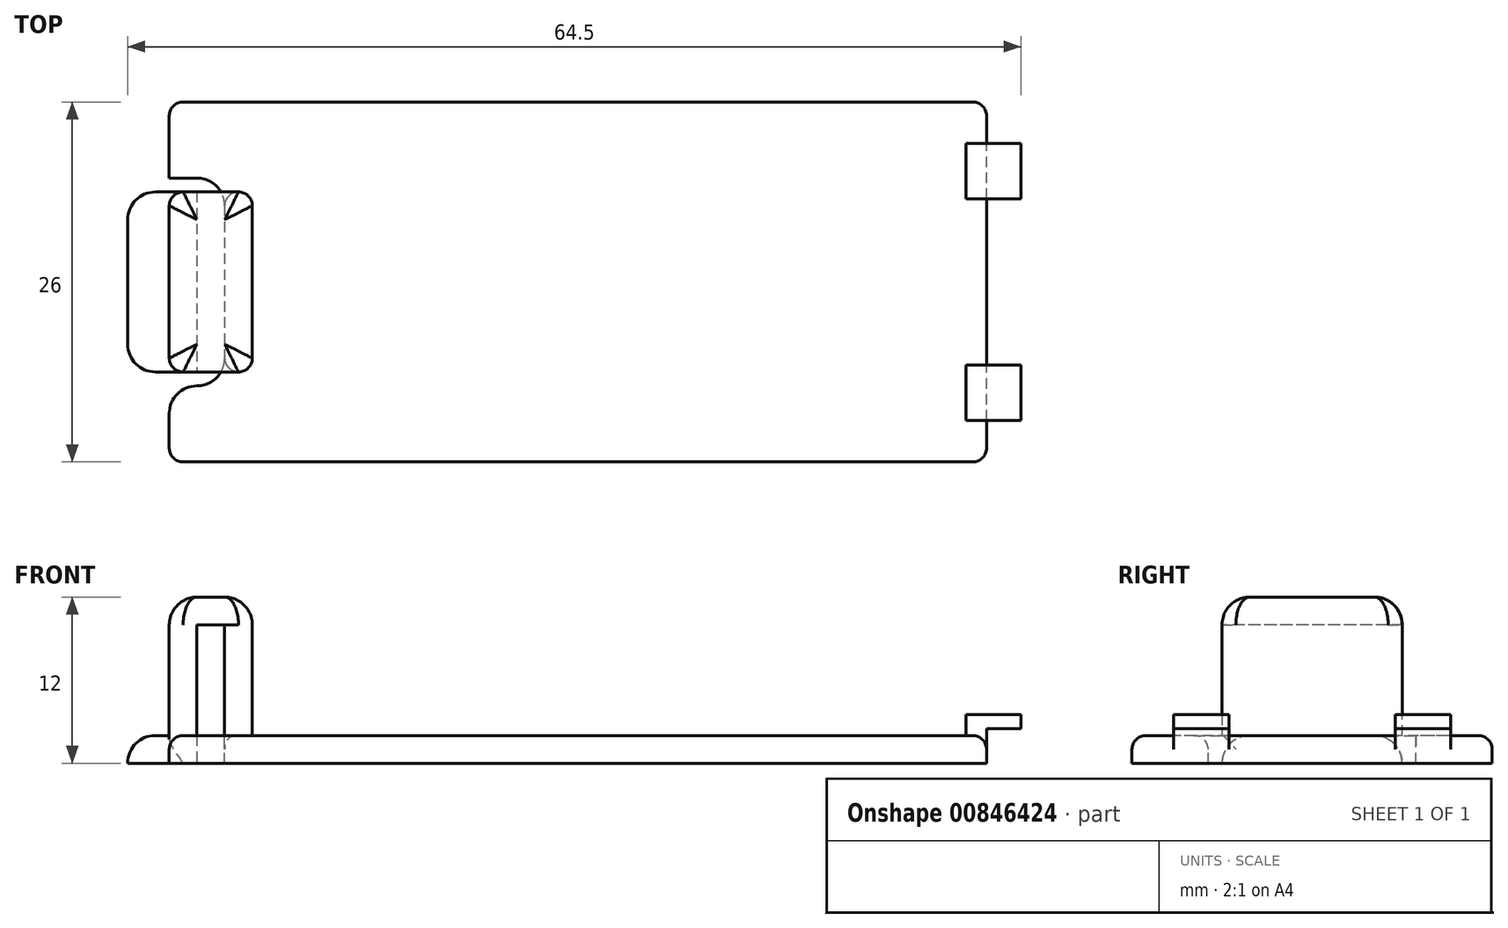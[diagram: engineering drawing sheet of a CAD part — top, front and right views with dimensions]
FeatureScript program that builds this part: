
annotation { "Feature Type Name" : "Feature", "Feature Type Description" : "" }
export const myFeature = defineFeature(function(context is Context, id is Id, definition is map)
    precondition{}
    {
        {
            var Q0;
            Q0=qCreatedBy(makeId("Top.planeOp"),FACE);
            var sketch = newSketch(context, id + "F0", { "sketchPlane" : qUnion([Q0])});
            skLineSegment(sketch, "E0.bottom", {"start": v(28.5, 13) * mm, "end": v(-28.5, 13) * mm});
            skLineSegment(sketch, "E0.top", {"start": v(28.5, -13) * mm, "end": v(-28.5, -13) * mm});
            skLineSegment(sketch, "E0.left", {"start": v(29.5, 12) * mm, "end": v(29.5, -12) * mm});
            skLineSegment(sketch, "E0.right", {"start": v(-29.5, 12) * mm, "end": v(-29.5, -12) * mm});
            skPoint(sketch, "E0.middle", {"position": v(0, 0) * mm});
            skPoint(sketch, "E1.visualSharp", {"position": v(-29.5, 13) * mm});
            skArc(sketch, "E1.filletArc", {"start": v(-28.5, 13) * mm, "mid": v(-29.2, 12.7) * mm, "end": v(-29.5, 12) * mm});
            skPoint(sketch, "E2.visualSharp", {"position": v(29.5, 13) * mm});
            skArc(sketch, "E2.filletArc", {"start": v(29.5, 12) * mm, "mid": v(29.2, 12.7) * mm, "end": v(28.5, 13) * mm});
            skPoint(sketch, "E3.visualSharp", {"position": v(29.5, -13) * mm});
            skArc(sketch, "E3.filletArc", {"start": v(28.5, -13) * mm, "mid": v(29.2, -12.7) * mm, "end": v(29.5, -12) * mm});
            skPoint(sketch, "E4.visualSharp", {"position": v(-29.5, -13) * mm});
            skArc(sketch, "E4.filletArc", {"start": v(-29.5, -12) * mm, "mid": v(-29.2, -12.7) * mm, "end": v(-28.5, -13) * mm});
            skSolve(sketch);
        }
        {
            var Q0;
            Q0=makeQuery(id+"F0.imprint","IMPRINT",FACE,{"disambiguationData":[TD([[makeQuery(id+"F0.imprint","IMPRINT",EDGE,{"derivedFrom":sQuery(id+"F0.wireOp",EDGE,"E0.bottom")}),1.0]])]});
            extrude(context, id + "F1", {"entities" : qUnion([Q0]), "depth" : 2 * mm, "offsetDistance" : 25 * mm});
        }
        {
            var Q0;
            Q0=makeQuery(id+"F1.opExtrude","CAP_FACE",FACE,{"disambiguationData":[OSD([sQuery(id+"F0.wireOp",EDGE,"E0.bottom"),sQuery(id+"F0.wireOp",EDGE,"E0.top"),sQuery(id+"F0.wireOp",EDGE,"E0.left"),sQuery(id+"F0.wireOp",EDGE,"E0.right"),sQuery(id+"F0.wireOp",EDGE,"E1.filletArc"),sQuery(id+"F0.wireOp",EDGE,"E2.filletArc"),sQuery(id+"F0.wireOp",EDGE,"E3.filletArc"),sQuery(id+"F0.wireOp",EDGE,"E4.filletArc")])],"isStart":false});
            var sketch = newSketch(context, id + "F2", { "sketchPlane" : qUnion([Q0])});
            skLineSegment(sketch, "E5.bottom", {"start": v(-23.5, 6.5) * mm, "end": v(-29.5, 6.5) * mm});
            skLineSegment(sketch, "E5.top", {"start": v(-23.5, -6.5) * mm, "end": v(-29.5, -6.5) * mm});
            skLineSegment(sketch, "E5.left", {"start": v(-23.5, 6.5) * mm, "end": v(-23.5, -6.5) * mm});
            skLineSegment(sketch, "E5.right", {"start": v(-29.5, 6.5) * mm, "end": v(-29.5, -6.5) * mm});
            skPoint(sketch, "E5.middle", {"position": v(-26.5, 0) * mm});
            skSolve(sketch);
        }
        {
            var Q0;
            Q0=makeQuery(id+"F2.imprint","IMPRINT",FACE,{"disambiguationData":[TD([[makeQuery(id+"F2.imprint","IMPRINT",EDGE,{"derivedFrom":sQuery(id+"F2.wireOp",EDGE,"E5.bottom")}),1.0]])]});
            extrude(context, id + "F3", {"entities" : qUnion([Q0]), "operationType" : NewBodyOperationType.ADD, "depth" : 10 * mm, "offsetDistance" : 25 * mm});
        }
        {
            var Q0;
            Q0=makeQuery(id+"F1.opExtrude","CAP_FACE",FACE,{"disambiguationData":[OSD([sQuery(id+"F0.wireOp",EDGE,"E0.bottom"),sQuery(id+"F0.wireOp",EDGE,"E0.top"),sQuery(id+"F0.wireOp",EDGE,"E0.left"),sQuery(id+"F0.wireOp",EDGE,"E0.right"),sQuery(id+"F0.wireOp",EDGE,"E1.filletArc"),sQuery(id+"F0.wireOp",EDGE,"E2.filletArc"),sQuery(id+"F0.wireOp",EDGE,"E3.filletArc"),sQuery(id+"F0.wireOp",EDGE,"E4.filletArc")])],"isStart":false});
            var sketch = newSketch(context, id + "F4", { "sketchPlane" : qUnion([Q0])});
            skLineSegment(sketch, "E6.bottom", {"start": v(-29.5, 6.5) * mm, "end": v(-25.5, 6.5) * mm});
            skLineSegment(sketch, "E6.top", {"start": v(-29.5, 7.5) * mm, "end": v(-25.5, 7.5) * mm});
            skLineSegment(sketch, "E6.left", {"start": v(-29.5, 6.5) * mm, "end": v(-29.5, 7.5) * mm});
            skLineSegment(sketch, "E6.right", {"start": v(-25.5, 6.5) * mm, "end": v(-25.5, 7.5) * mm});
            skLineSegment(sketch, "E7.bottom", {"start": v(-29.5, -6.5) * mm, "end": v(-25.5, -6.5) * mm});
            skLineSegment(sketch, "E7.top", {"start": v(-29.5, -7.5) * mm, "end": v(-25.5, -7.5) * mm});
            skLineSegment(sketch, "E7.left", {"start": v(-29.5, -6.5) * mm, "end": v(-29.5, -7.5) * mm});
            skLineSegment(sketch, "E7.right", {"start": v(-25.5, -6.5) * mm, "end": v(-25.5, -7.5) * mm});
            skSolve(sketch);
        }
        {
            var Q0;
            Q0=makeQuery(id+"F4.imprint","IMPRINT",FACE,{"disambiguationData":[TD([[makeQuery(id+"F4.imprint","IMPRINT",EDGE,{"derivedFrom":sQuery(id+"F4.wireOp",EDGE,"E6.bottom")}),-1.0]])]});
            var Q1;
            Q1=makeQuery(id+"F4.imprint","IMPRINT",FACE,{"disambiguationData":[TD([[makeQuery(id+"F4.imprint","IMPRINT",EDGE,{"derivedFrom":sQuery(id+"F4.wireOp",EDGE,"E7.bottom")}),1.0]])]});
            extrude(context, id + "F5", {"entities" : qUnion([Q0, Q1]), "operationType" : NewBodyOperationType.REMOVE, "oppositeDirection" : true, "depth" : 25 * mm, "offsetDistance" : 25 * mm});
        }
        {
            var Q0;
            {var subQ0=sQuery(id+"F2.wireOp",EDGE,"E5.right");var subQ2=sQuery(id+"F2.wireOp",EDGE,"E5.bottom");var subQ3=sQuery(id+"F0.wireOp",EDGE,"E0.right");Q0=makeQuery(id+"F5.boolean.opBoolean","SPLIT",FACE,{"disambiguationData":[TD([makeQuery(id+"F3.opExtrude","SWEPT_FACE",FACE,{"disambiguationData":[OSD([subQ2])]})])],"derivedFrom":makeQuery(id+"F3.boolean.opBoolean","MERGE",FACE,{"derivedFrom":[makeQuery(id+"F1.opExtrude","SWEPT_FACE",FACE,{"disambiguationData":[OSD([subQ3])]}),makeQuery(id+"F3.opExtrude","SWEPT_FACE",FACE,{"disambiguationData":[OSD([subQ0])]})]})});}
            var sketch = newSketch(context, id + "F6", { "sketchPlane" : qUnion([Q0])});
            skLineSegment(sketch, "E8.bottom", {"start": v(-6.5, 0) * mm, "end": v(6.5, 0) * mm});
            skLineSegment(sketch, "E8.top", {"start": v(-4.5, 2) * mm, "end": v(4.5, 2) * mm});
            skLineSegment(sketch, "E8.left", {"start": v(-6.5, 0) * mm, "end": v(-6.5, 0) * mm});
            skLineSegment(sketch, "E8.right", {"start": v(6.5, 0) * mm, "end": v(6.5, 0) * mm});
            skPoint(sketch, "E9.visualSharp", {"position": v(-6.5, 2) * mm});
            skArc(sketch, "E9.filletArc", {"start": v(-4.5, 2) * mm, "mid": v(-5.91, 1.41) * mm, "end": v(-6.5, 0) * mm});
            skPoint(sketch, "E10.visualSharp", {"position": v(6.5, 2) * mm});
            skArc(sketch, "E10.filletArc", {"start": v(6.5, 0) * mm, "mid": v(5.91, 1.41) * mm, "end": v(4.5, 2) * mm});
            skSolve(sketch);
        }
        {
            var Q0;
            Q0=makeQuery(id+"F6.imprint","IMPRINT",FACE,{"disambiguationData":[TD([[makeQuery(id+"F6.imprint","IMPRINT",EDGE,{"derivedFrom":sQuery(id+"F6.wireOp",EDGE,"E8.bottom")}),1.0]])]});
            extrude(context, id + "F7", {"entities" : qUnion([Q0]), "operationType" : NewBodyOperationType.ADD, "depth" : 3 * mm, "offsetDistance" : 25 * mm});
        }
        {
            var Q0;
            Q0=makeQuery(id+"F5.boolean.opBoolean","MERGE",FACE,{"derivedFrom":[makeQuery(id+"F3.opExtrude","SWEPT_FACE",FACE,{"disambiguationData":[OSD([sQuery(id+"F2.wireOp",EDGE,"E5.top")])]}),makeQuery(id+"F5.opExtrude","SWEPT_FACE",FACE,{"disambiguationData":[OSD([sQuery(id+"F4.wireOp",EDGE,"ozfxwtHF-AlxI-n3KI-FFb6-HUCzDKYGf8rM.bottom")])]})]});
            var sketch = newSketch(context, id + "F8", { "sketchPlane" : qUnion([Q0])});
            skLineSegment(sketch, "E11.bottom", {"start": v(-27.5, 10) * mm, "end": v(-25.5, 10) * mm});
            skLineSegment(sketch, "E11.top", {"start": v(-27.5, 0) * mm, "end": v(-25.5, 0) * mm});
            skLineSegment(sketch, "E11.left", {"start": v(-27.5, 10) * mm, "end": v(-27.5, 0) * mm});
            skLineSegment(sketch, "E11.right", {"start": v(-25.5, 10) * mm, "end": v(-25.5, 0) * mm});
            skSolve(sketch);
        }
        {
            var Q0;
            Q0=makeQuery(id+"F8.imprint","IMPRINT",FACE,{"disambiguationData":[TD([[makeQuery(id+"F8.imprint","IMPRINT",EDGE,{"derivedFrom":sQuery(id+"F8.wireOp",EDGE,"E11.bottom")}),-1.0]])]});
            var Q1;
            Q1=makeQuery(id+"F5.boolean.opBoolean","MERGE",FACE,{"derivedFrom":[makeQuery(id+"F3.opExtrude","SWEPT_FACE",FACE,{"disambiguationData":[OSD([sQuery(id+"F2.wireOp",EDGE,"E5.bottom")])]}),makeQuery(id+"F5.opExtrude","SWEPT_FACE",FACE,{"disambiguationData":[OSD([sQuery(id+"F4.wireOp",EDGE,"34y3R7rX-EJcI-0oel-cIUl-SeJOH7LNdRKQ.bottom")])]})]});
            extrude(context, id + "F9", {"entities" : qUnion([Q0]), "operationType" : NewBodyOperationType.REMOVE, "endBound" : BoundingType.UP_TO_SURFACE, "oppositeDirection" : true, "depth" : 12 * mm, "endBoundEntityFace" : qUnion([Q1]), "offsetDistance" : 25 * mm});
        }
        {
            var Q0;
            Q0=makeQuery(id+"F5.boolean.opBoolean","COPY",EDGE,{"derivedFrom":makeQuery(id+"F5.opExtrude","SWEPT_EDGE",EDGE,{"disambiguationData":[OSD([sQuery(id+"F4.wireOp",EDGE,"E7.top"),sQuery(id+"F4.wireOp",EDGE,"E7.right")])]})});
            var Q1;
            Q1=makeQuery(id+"F5.boolean.opBoolean","COPY",EDGE,{"derivedFrom":makeQuery(id+"F5.opExtrude","SWEPT_EDGE",EDGE,{"disambiguationData":[OSD([sQuery(id+"F4.wireOp",EDGE,"E6.top"),sQuery(id+"F4.wireOp",EDGE,"E6.right")])]})});
            var Q2;
            Q2=makeQuery(id+"F5.boolean.opBoolean","COPY",EDGE,{"derivedFrom":makeQuery(id+"F5.opExtrude","SWEPT_EDGE",EDGE,{"disambiguationData":[OSD([sQuery(id+"F0.wireOp",EDGE,"E0.right"),sQuery(id+"F4.wireOp",EDGE,"E7.top"),sQuery(id+"F4.wireOp",EDGE,"E7.left")])]})});
            var Q3;
            Q3=makeQuery(id+"F5.boolean.opBoolean","COPY",EDGE,{"derivedFrom":makeQuery(id+"F5.opExtrude","SWEPT_EDGE",EDGE,{"disambiguationData":[OSD([sQuery(id+"F0.wireOp",EDGE,"E0.right"),sQuery(id+"F4.wireOp",EDGE,"E6.top"),sQuery(id+"F4.wireOp",EDGE,"E6.left")])]})});
            fillet(context, id + "F10", {"entities" : qUnion([Q0, Q1, Q2, Q3]), "radius" : 2 * mm, "tangentPropagation" : true, "allowEdgeOverflow" : false});
        }
        {
            var Q0;
            Q0=makeQuery(id+"F9.boolean.opBoolean","COPY",EDGE,{"derivedFrom":makeQuery(id+"F9.opExtrude","CAP_EDGE",EDGE,{"disambiguationData":[OSD([sQuery(id+"F8.wireOp",EDGE,"E11.left")])],"isStart":true})});
            var Q1;
            Q1=makeQuery(id+"F9.boolean.opBoolean","COPY",EDGE,{"derivedFrom":makeQuery(id+"F9.opExtrude","CAP_EDGE",EDGE,{"disambiguationData":[OSD([sQuery(id+"F8.wireOp",EDGE,"E11.left")])],"isStart":false})});
            var Q2;
            Q2=makeQuery(id+"F5.boolean.opBoolean","MERGE",EDGE,{"derivedFrom":[makeQuery(id+"F3.opExtrude","SWEPT_EDGE",EDGE,{"disambiguationData":[OSD([sQuery(id+"F0.wireOp",EDGE,"E0.right"),sQuery(id+"F2.wireOp",EDGE,"E5.bottom"),sQuery(id+"F2.wireOp",EDGE,"E5.right")])]}),makeQuery(id+"F5.opExtrude","SWEPT_EDGE",EDGE,{"disambiguationData":[OSD([sQuery(id+"F4.wireOp",EDGE,"E6.bottom"),sQuery(id+"F4.wireOp",EDGE,"E6.left")])]})]});
            var Q3;
            Q3=makeQuery(id+"F5.boolean.opBoolean","MERGE",EDGE,{"derivedFrom":[makeQuery(id+"F3.opExtrude","SWEPT_EDGE",EDGE,{"disambiguationData":[OSD([sQuery(id+"F0.wireOp",EDGE,"E0.right"),sQuery(id+"F2.wireOp",EDGE,"E5.top"),sQuery(id+"F2.wireOp",EDGE,"E5.right")])]}),makeQuery(id+"F5.opExtrude","SWEPT_EDGE",EDGE,{"disambiguationData":[OSD([sQuery(id+"F4.wireOp",EDGE,"E7.bottom"),sQuery(id+"F4.wireOp",EDGE,"E7.left")])]})]});
            var Q4;
            Q4=makeQuery(id+"F10.opFillet","BLEND_EDGE",EDGE,{"blendedFrom":[makeQuery(id+"F5.boolean.opBoolean","COPY",EDGE,{"derivedFrom":makeQuery(id+"F5.opExtrude","SWEPT_EDGE",EDGE,{"disambiguationData":[OSD([sQuery(id+"F4.wireOp",EDGE,"E6.top"),sQuery(id+"F4.wireOp",EDGE,"E6.right")])]})}),makeQuery(id+"F5.boolean.opBoolean","MERGE",FACE,{"derivedFrom":[makeQuery(id+"F3.opExtrude","SWEPT_FACE",FACE,{"disambiguationData":[OSD([sQuery(id+"F2.wireOp",EDGE,"E5.bottom")])]}),makeQuery(id+"F5.opExtrude","SWEPT_FACE",FACE,{"disambiguationData":[OSD([sQuery(id+"F4.wireOp",EDGE,"E6.bottom")])]})]})],"blendedInto":[makeQuery(id+"F5.boolean.opBoolean","MERGE",FACE,{"derivedFrom":[makeQuery(id+"F3.opExtrude","SWEPT_FACE",FACE,{"disambiguationData":[OSD([sQuery(id+"F2.wireOp",EDGE,"E5.bottom")])]}),makeQuery(id+"F5.opExtrude","SWEPT_FACE",FACE,{"disambiguationData":[OSD([sQuery(id+"F4.wireOp",EDGE,"E6.bottom")])]})]})]});
            var Q5;
            Q5=makeQuery(id+"F10.opFillet","BLEND_EDGE",EDGE,{"blendedFrom":[makeQuery(id+"F5.boolean.opBoolean","COPY",EDGE,{"derivedFrom":makeQuery(id+"F5.opExtrude","SWEPT_EDGE",EDGE,{"disambiguationData":[OSD([sQuery(id+"F4.wireOp",EDGE,"E7.top"),sQuery(id+"F4.wireOp",EDGE,"E7.right")])]})}),makeQuery(id+"F5.boolean.opBoolean","MERGE",FACE,{"derivedFrom":[makeQuery(id+"F3.opExtrude","SWEPT_FACE",FACE,{"disambiguationData":[OSD([sQuery(id+"F2.wireOp",EDGE,"E5.top")])]}),makeQuery(id+"F5.opExtrude","SWEPT_FACE",FACE,{"disambiguationData":[OSD([sQuery(id+"F4.wireOp",EDGE,"E7.bottom")])]})]})],"blendedInto":[makeQuery(id+"F5.boolean.opBoolean","MERGE",FACE,{"derivedFrom":[makeQuery(id+"F3.opExtrude","SWEPT_FACE",FACE,{"disambiguationData":[OSD([sQuery(id+"F2.wireOp",EDGE,"E5.top")])]}),makeQuery(id+"F5.opExtrude","SWEPT_FACE",FACE,{"disambiguationData":[OSD([sQuery(id+"F4.wireOp",EDGE,"E7.bottom")])]})]})]});
            var Q6;
            Q6=makeQuery(id+"F3.opExtrude","SWEPT_EDGE",EDGE,{"disambiguationData":[OSD([sQuery(id+"F2.wireOp",EDGE,"E5.bottom"),sQuery(id+"F2.wireOp",EDGE,"E5.left")])]});
            var Q7;
            Q7=makeQuery(id+"F3.opExtrude","SWEPT_EDGE",EDGE,{"disambiguationData":[OSD([sQuery(id+"F2.wireOp",EDGE,"E5.top"),sQuery(id+"F2.wireOp",EDGE,"E5.left")])]});
            fillet(context, id + "F11", {"entities" : qUnion([Q0, Q1, Q2, Q3, Q4, Q5, Q6, Q7]), "radius" : 1 * mm, "tangentPropagation" : true, "allowEdgeOverflow" : false});
        }
        {
            var Q0;
            Q0=makeQuery(id+"F3.opExtrude","CAP_EDGE",EDGE,{"disambiguationData":[OSD([sQuery(id+"F2.wireOp",EDGE,"E5.right")])],"isStart":false});
            var Q1;
            Q1=makeQuery(id+"F3.opExtrude","CAP_EDGE",EDGE,{"disambiguationData":[OSD([sQuery(id+"F2.wireOp",EDGE,"E5.left")])],"isStart":false});
            var Q2;
            Q2=makeQuery(id+"F7.opExtrude","CAP_EDGE",EDGE,{"disambiguationData":[OSD([sQuery(id+"F6.wireOp",EDGE,"E8.top")])],"isStart":false});
            fillet(context, id + "F12", {"entities" : qUnion([Q0, Q1, Q2]), "radius" : 2 * mm, "tangentPropagation" : true, "allowEdgeOverflow" : false});
        }
        {
            var Q0;
            Q0=makeQuery(id+"F1.opExtrude","CAP_FACE",FACE,{"disambiguationData":[OSD([sQuery(id+"F0.wireOp",EDGE,"E0.bottom"),sQuery(id+"F0.wireOp",EDGE,"E0.top"),sQuery(id+"F0.wireOp",EDGE,"E0.left"),sQuery(id+"F0.wireOp",EDGE,"E0.right"),sQuery(id+"F0.wireOp",EDGE,"E1.filletArc"),sQuery(id+"F0.wireOp",EDGE,"E2.filletArc"),sQuery(id+"F0.wireOp",EDGE,"E3.filletArc"),sQuery(id+"F0.wireOp",EDGE,"E4.filletArc")])],"isStart":false});
            var sketch = newSketch(context, id + "F13", { "sketchPlane" : qUnion([Q0])});
            skLineSegment(sketch, "E12.bottom", {"start": v(29.5, 10) * mm, "end": v(28, 10) * mm});
            skLineSegment(sketch, "E12.top", {"start": v(29.5, 6) * mm, "end": v(28, 6) * mm});
            skLineSegment(sketch, "E12.left", {"start": v(29.5, 10) * mm, "end": v(29.5, 6) * mm});
            skLineSegment(sketch, "E12.right", {"start": v(28, 10) * mm, "end": v(28, 6) * mm});
            skLineSegment(sketch, "E13.bottom", {"start": v(29.5, -6) * mm, "end": v(28, -6) * mm});
            skLineSegment(sketch, "E13.top", {"start": v(29.5, -10) * mm, "end": v(28, -10) * mm});
            skLineSegment(sketch, "E13.left", {"start": v(29.5, -6) * mm, "end": v(29.5, -10) * mm});
            skLineSegment(sketch, "E13.right", {"start": v(28, -6) * mm, "end": v(28, -10) * mm});
            skSolve(sketch);
        }
        {
            var Q0;
            Q0=makeQuery(id+"F13.imprint","IMPRINT",FACE,{"disambiguationData":[TD([[makeQuery(id+"F13.imprint","IMPRINT",EDGE,{"derivedFrom":sQuery(id+"F13.wireOp",EDGE,"E12.bottom")}),1.0]])]});
            var Q1;
            Q1=makeQuery(id+"F13.imprint","IMPRINT",FACE,{"disambiguationData":[TD([[makeQuery(id+"F13.imprint","IMPRINT",EDGE,{"derivedFrom":sQuery(id+"F13.wireOp",EDGE,"E13.bottom")}),1.0]])]});
            extrude(context, id + "F14", {"entities" : qUnion([Q0, Q1]), "operationType" : NewBodyOperationType.ADD, "depth" : 1.5 * mm, "offsetDistance" : 25 * mm});
        }
        {
            var Q0;
            Q0=makeQuery(id+"F14.boolean.opBoolean","MERGE",FACE,{"derivedFrom":[makeQuery(id+"F1.opExtrude","SWEPT_FACE",FACE,{"disambiguationData":[OSD([sQuery(id+"F0.wireOp",EDGE,"E0.left")])]}),makeQuery(id+"F14.opExtrude","SWEPT_FACE",FACE,{"disambiguationData":[OSD([sQuery(id+"F13.wireOp",EDGE,"E12.left")])]}),makeQuery(id+"F14.opExtrude","SWEPT_FACE",FACE,{"disambiguationData":[OSD([sQuery(id+"F13.wireOp",EDGE,"E13.left")])]})]});
            var sketch = newSketch(context, id + "F15", { "sketchPlane" : qUnion([Q0])});
            skLineSegment(sketch, "E14.bottom", {"start": v(-10, 3.5) * mm, "end": v(-6, 3.5) * mm});
            skLineSegment(sketch, "E14.top", {"start": v(-10, 2.5) * mm, "end": v(-6, 2.5) * mm});
            skLineSegment(sketch, "E14.left", {"start": v(-10, 3.5) * mm, "end": v(-10, 2.5) * mm});
            skLineSegment(sketch, "E14.right", {"start": v(-6, 3.5) * mm, "end": v(-6, 2.5) * mm});
            skLineSegment(sketch, "E15.bottom", {"start": v(6, 3.5) * mm, "end": v(10, 3.5) * mm});
            skLineSegment(sketch, "E15.top", {"start": v(6, 2.5) * mm, "end": v(10, 2.5) * mm});
            skLineSegment(sketch, "E15.left", {"start": v(6, 3.5) * mm, "end": v(6, 2.5) * mm});
            skLineSegment(sketch, "E15.right", {"start": v(10, 3.5) * mm, "end": v(10, 2.5) * mm});
            skSolve(sketch);
        }
        {
            var Q0;
            Q0=makeQuery(id+"F15.imprint","IMPRINT",FACE,{"disambiguationData":[TD([[makeQuery(id+"F15.imprint","IMPRINT",EDGE,{"derivedFrom":sQuery(id+"F15.wireOp",EDGE,"E14.bottom")}),1.0]])]});
            var Q1;
            Q1=makeQuery(id+"F15.imprint","IMPRINT",FACE,{"disambiguationData":[TD([[makeQuery(id+"F15.imprint","IMPRINT",EDGE,{"derivedFrom":sQuery(id+"F15.wireOp",EDGE,"E15.bottom")}),1.0]])]});
            extrude(context, id + "F16", {"entities" : qUnion([Q0, Q1]), "operationType" : NewBodyOperationType.ADD, "depth" : 2.5 * mm, "offsetDistance" : 25 * mm});
        }
        {
            var Q0;
            Q0=makeQuery(id+"F1.opExtrude","CAP_EDGE",EDGE,{"disambiguationData":[OSD([sQuery(id+"F0.wireOp",EDGE,"E0.bottom")])],"isStart":false});
            var Q1;
            Q1=makeQuery(id+"F1.opExtrude","CAP_EDGE",EDGE,{"disambiguationData":[OSD([sQuery(id+"F0.wireOp",EDGE,"E0.top")])],"isStart":false});
            var Q2;
            {var subQ0=sQuery(id+"F0.wireOp",EDGE,"E0.left");Q2=makeQuery(id+"F14.boolean.opBoolean","SPLIT",EDGE,{"disambiguationData":[TD([makeQuery(id+"F14.opExtrude","SWEPT_FACE",FACE,{"disambiguationData":[OSD([sQuery(id+"F13.wireOp",EDGE,"E12.top")])]})])],"derivedFrom":makeQuery(id+"F1.opExtrude","CAP_EDGE",EDGE,{"disambiguationData":[OSD([subQ0])],"isStart":false})});}
            fillet(context, id + "F17", {"entities" : qUnion([Q0, Q1, Q2]), "radius" : 1 * mm, "tangentPropagation" : true, "allowEdgeOverflow" : false});
        }
    });
